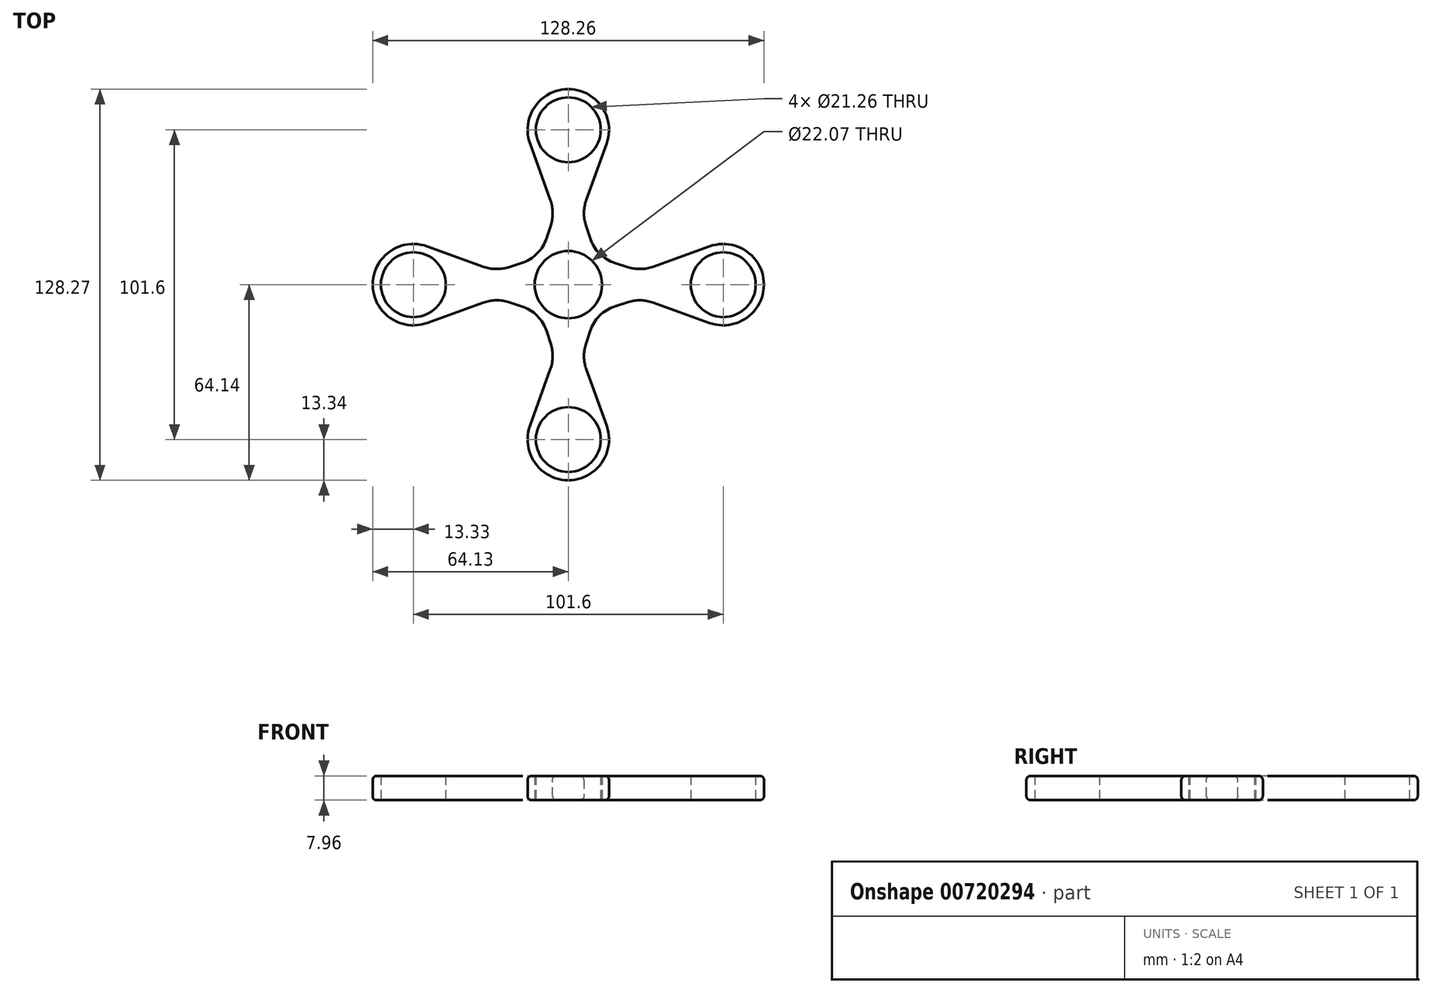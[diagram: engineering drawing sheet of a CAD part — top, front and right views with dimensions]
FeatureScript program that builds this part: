
annotation { "Feature Type Name" : "Feature", "Feature Type Description" : "" }
export const myFeature = defineFeature(function(context is Context, id is Id, definition is map)
    precondition{}
    {
        {
            var Q0;
            Q0=qCreatedBy(makeId("Top.planeOp"),FACE);
            var sketch = newSketch(context, id + "F0", { "sketchPlane" : qUnion([Q0])});
            skCircle(sketch, "E0", {"center": v(0, 0) * mm, "radius": 11.43 * mm});
            skCircle(sketch, "E1", {"center": v(0, 50.8) * mm, "radius": 13.34 * mm});
            skCircle(sketch, "E2", {"center": v(-50.8, 0) * mm, "radius": 13.34 * mm});
            skCircle(sketch, "E3", {"center": v(0, -50.8) * mm, "radius": 13.34 * mm});
            skCircle(sketch, "E4", {"center": v(50.8, 0) * mm, "radius": 13.34 * mm});
            skLineSegment(sketch, "E5", {"start": v(0, 37.47) * mm, "end": v(-10.89, 3.49) * mm});
            skLineSegment(sketch, "E6", {"start": v(0, 37.47) * mm, "end": v(10.89, 3.49) * mm});
            skLineSegment(sketch, "E7", {"start": v(-12.55, 46.28) * mm, "end": v(0, 11.43) * mm});
            skLineSegment(sketch, "E8", {"start": v(0, 11.43) * mm, "end": v(12.55, 46.28) * mm});
            skLineSegment(sketch, "E9", {"start": v(-46.28, 12.55) * mm, "end": v(-11.43, 0) * mm});
            skLineSegment(sketch, "E10", {"start": v(-11.43, 0) * mm, "end": v(-46.28, -12.55) * mm});
            skLineSegment(sketch, "E11", {"start": v(-37.46, 0) * mm, "end": v(-3.49, 10.89) * mm});
            skLineSegment(sketch, "E12", {"start": v(-37.47, 0) * mm, "end": v(-3.49, -10.89) * mm});
            skLineSegment(sketch, "E13", {"start": v(-12.55, -46.28) * mm, "end": v(0, -11.43) * mm});
            skLineSegment(sketch, "E14", {"start": v(0, -11.43) * mm, "end": v(12.55, -46.28) * mm});
            skLineSegment(sketch, "E15", {"start": v(-10.89, -3.49) * mm, "end": v(0, -37.47) * mm});
            skLineSegment(sketch, "E16", {"start": v(0, -37.46) * mm, "end": v(10.89, -3.49) * mm});
            skLineSegment(sketch, "E17", {"start": v(37.47, 0) * mm, "end": v(3.49, 10.89) * mm});
            skLineSegment(sketch, "E18", {"start": v(3.49, -10.89) * mm, "end": v(37.47, 0) * mm});
            skLineSegment(sketch, "E19", {"start": v(11.43, 0) * mm, "end": v(46.28, 12.55) * mm});
            skLineSegment(sketch, "E20", {"start": v(11.43, 0) * mm, "end": v(46.28, -12.55) * mm});
            skLineSegment(sketch, "E21", {"start": v(0, 50.8) * mm, "end": v(0, 0) * mm});
            skLineSegment(sketch, "E22", {"start": v(0, 0) * mm, "end": v(-50.8, 0) * mm});
            skLineSegment(sketch, "E23", {"start": v(0, 0) * mm, "end": v(0, -50.8) * mm});
            skLineSegment(sketch, "E24", {"start": v(0, 0) * mm, "end": v(50.8, 0) * mm});
            skSolve(sketch);
        }
        {
            var Q0;
            {var subQ0=sQuery(id+"F0.wireOp",EDGE,"E1");var subQ2=makeQuery(id+"F0.imprint","INTERSECT",VERTEX,{"derivedFrom":[subQ0,sQuery(id+"F0.wireOp",EDGE,"E7")]});Q0=makeQuery(id+"F0.imprint","IMPRINT",FACE,{"disambiguationData":[TD([[makeQuery(id+"F0.imprint","IMPRINT",EDGE,{"disambiguationData":[TD([[subQ2,1.0]])],"derivedFrom":subQ0}),1.0]])]});}
            var Q1;
            {var subQ1=sQuery(id+"F0.wireOp",EDGE,"E1");var subQ3=sQuery(id+"F0.wireOp",EDGE,"E7");var subQ4=makeQuery(id+"F0.imprint","INTERSECT",VERTEX,{"derivedFrom":[subQ1,subQ3]});Q1=makeQuery(id+"F0.imprint","IMPRINT",FACE,{"disambiguationData":[TD([[makeQuery(id+"F0.imprint","IMPRINT",EDGE,{"disambiguationData":[TD([[subQ4,-1.0]])],"derivedFrom":subQ3}),1.0]])]});}
            var Q2;
            {var subQ1=sQuery(id+"F0.wireOp",EDGE,"E1");var subQ3=sQuery(id+"F0.wireOp",EDGE,"E8");var subQ4=makeQuery(id+"F0.imprint","INTERSECT",VERTEX,{"derivedFrom":[subQ1,subQ3]});Q2=makeQuery(id+"F0.imprint","IMPRINT",FACE,{"disambiguationData":[TD([[makeQuery(id+"F0.imprint","IMPRINT",EDGE,{"disambiguationData":[TD([[subQ4,1.0]])],"derivedFrom":subQ3}),1.0]])]});}
            var Q3;
            {var subQ0=sQuery(id+"F0.wireOp",EDGE,"E9");var subQ1=sQuery(id+"F0.wireOp",EDGE,"E2");var subQ2=makeQuery(id+"F0.imprint","INTERSECT",VERTEX,{"derivedFrom":[subQ1,subQ0]});Q3=makeQuery(id+"F0.imprint","IMPRINT",FACE,{"disambiguationData":[TD([[makeQuery(id+"F0.imprint","IMPRINT",EDGE,{"disambiguationData":[TD([[subQ2,-1.0]])],"derivedFrom":subQ0}),-1.0]])]});}
            var Q4;
            {var subQ0=sQuery(id+"F0.wireOp",EDGE,"E10");var subQ1=sQuery(id+"F0.wireOp",EDGE,"E2");var subQ2=makeQuery(id+"F0.imprint","INTERSECT",VERTEX,{"derivedFrom":[subQ1,subQ0]});Q4=makeQuery(id+"F0.imprint","IMPRINT",FACE,{"disambiguationData":[TD([[makeQuery(id+"F0.imprint","IMPRINT",EDGE,{"disambiguationData":[TD([[subQ2,1.0]])],"derivedFrom":subQ0}),-1.0]])]});}
            var Q5;
            {var subQ0=sQuery(id+"F0.wireOp",EDGE,"E3");var subQ3=makeQuery(id+"F0.imprint","INTERSECT",VERTEX,{"derivedFrom":[subQ0,sQuery(id+"F0.wireOp",EDGE,"E13")]});Q5=makeQuery(id+"F0.imprint","IMPRINT",FACE,{"disambiguationData":[TD([[makeQuery(id+"F0.imprint","IMPRINT",EDGE,{"disambiguationData":[TD([[subQ3,-1.0]])],"derivedFrom":subQ0}),1.0]])]});}
            var Q6;
            {var subQ0=sQuery(id+"F0.wireOp",EDGE,"E14");var subQ1=sQuery(id+"F0.wireOp",EDGE,"E3");var subQ2=makeQuery(id+"F0.imprint","INTERSECT",VERTEX,{"derivedFrom":[subQ1,subQ0]});Q6=makeQuery(id+"F0.imprint","IMPRINT",FACE,{"disambiguationData":[TD([[makeQuery(id+"F0.imprint","IMPRINT",EDGE,{"disambiguationData":[TD([[subQ2,1.0]])],"derivedFrom":subQ0}),-1.0]])]});}
            var Q7;
            {var subQ0=sQuery(id+"F0.wireOp",EDGE,"E13");var subQ1=sQuery(id+"F0.wireOp",EDGE,"E3");var subQ2=makeQuery(id+"F0.imprint","INTERSECT",VERTEX,{"derivedFrom":[subQ1,subQ0]});Q7=makeQuery(id+"F0.imprint","IMPRINT",FACE,{"disambiguationData":[TD([[makeQuery(id+"F0.imprint","IMPRINT",EDGE,{"disambiguationData":[TD([[subQ2,-1.0]])],"derivedFrom":subQ0}),-1.0]])]});}
            var Q8;
            {var subQ0=sQuery(id+"F0.wireOp",EDGE,"E4");var subQ2=makeQuery(id+"F0.imprint","INTERSECT",VERTEX,{"derivedFrom":[subQ0,sQuery(id+"F0.wireOp",EDGE,"E19")]});Q8=makeQuery(id+"F0.imprint","IMPRINT",FACE,{"disambiguationData":[TD([[makeQuery(id+"F0.imprint","IMPRINT",EDGE,{"disambiguationData":[TD([[subQ2,1.0]])],"derivedFrom":subQ0}),1.0]])]});}
            var Q9;
            {var subQ1=sQuery(id+"F0.wireOp",EDGE,"E4");var subQ3=sQuery(id+"F0.wireOp",EDGE,"E19");var subQ4=makeQuery(id+"F0.imprint","INTERSECT",VERTEX,{"derivedFrom":[subQ1,subQ3]});Q9=makeQuery(id+"F0.imprint","IMPRINT",FACE,{"disambiguationData":[TD([[makeQuery(id+"F0.imprint","IMPRINT",EDGE,{"disambiguationData":[TD([[subQ4,1.0]])],"derivedFrom":subQ3}),-1.0]])]});}
            var Q10;
            {var subQ1=sQuery(id+"F0.wireOp",EDGE,"E4");var subQ3=sQuery(id+"F0.wireOp",EDGE,"E20");var subQ4=makeQuery(id+"F0.imprint","INTERSECT",VERTEX,{"derivedFrom":[subQ1,subQ3]});Q10=makeQuery(id+"F0.imprint","IMPRINT",FACE,{"disambiguationData":[TD([[makeQuery(id+"F0.imprint","IMPRINT",EDGE,{"disambiguationData":[TD([[subQ4,1.0]])],"derivedFrom":subQ3}),1.0]])]});}
            var Q11;
            {var subQ0=sQuery(id+"F0.wireOp",EDGE,"E6");var subQ1=sQuery(id+"F0.wireOp",EDGE,"E0");var subQ2=makeQuery(id+"F0.imprint","INTERSECT",VERTEX,{"derivedFrom":[subQ1,subQ0]});Q11=makeQuery(id+"F0.imprint","IMPRINT",FACE,{"disambiguationData":[TD([[makeQuery(id+"F0.imprint","IMPRINT",EDGE,{"disambiguationData":[TD([[subQ2,1.0]])],"derivedFrom":subQ0}),1.0]])]});}
            var Q12;
            {var subQ0=sQuery(id+"F0.wireOp",EDGE,"E6");var subQ1=sQuery(id+"F0.wireOp",EDGE,"E0");var subQ2=makeQuery(id+"F0.imprint","INTERSECT",VERTEX,{"derivedFrom":[subQ1,subQ0]});Q12=makeQuery(id+"F0.imprint","IMPRINT",FACE,{"disambiguationData":[TD([[makeQuery(id+"F0.imprint","IMPRINT",EDGE,{"disambiguationData":[TD([[subQ2,-1.0]])],"derivedFrom":subQ1}),-1.0]])]});}
            var Q13;
            {var subQ0=sQuery(id+"F0.wireOp",EDGE,"E8");var subQ5=sQuery(id+"F0.wireOp",EDGE,"E6");var subQ6=makeQuery(id+"F0.imprint","INTERSECT",VERTEX,{"derivedFrom":[subQ5,subQ0]});Q13=makeQuery(id+"F0.imprint","IMPRINT",FACE,{"disambiguationData":[TD([[makeQuery(id+"F0.imprint","IMPRINT",EDGE,{"disambiguationData":[TD([[subQ6,-1.0]])],"derivedFrom":subQ5}),-1.0]])]});}
            var Q14;
            {var subQ0=sQuery(id+"F0.wireOp",EDGE,"E7");var subQ5=sQuery(id+"F0.wireOp",EDGE,"E5");var subQ6=makeQuery(id+"F0.imprint","INTERSECT",VERTEX,{"derivedFrom":[subQ5,subQ0]});Q14=makeQuery(id+"F0.imprint","IMPRINT",FACE,{"disambiguationData":[TD([[makeQuery(id+"F0.imprint","IMPRINT",EDGE,{"disambiguationData":[TD([[subQ6,-1.0]])],"derivedFrom":subQ5}),1.0]])]});}
            var Q15;
            {var subQ0=sQuery(id+"F0.wireOp",EDGE,"E5");var subQ1=sQuery(id+"F0.wireOp",EDGE,"E0");var subQ2=makeQuery(id+"F0.imprint","INTERSECT",VERTEX,{"derivedFrom":[subQ1,subQ0]});Q15=makeQuery(id+"F0.imprint","IMPRINT",FACE,{"disambiguationData":[TD([[makeQuery(id+"F0.imprint","IMPRINT",EDGE,{"disambiguationData":[TD([[subQ2,1.0]])],"derivedFrom":subQ1}),-1.0]])]});}
            var Q16;
            {var subQ0=sQuery(id+"F0.wireOp",EDGE,"E5");var subQ1=sQuery(id+"F0.wireOp",EDGE,"E0");var subQ2=makeQuery(id+"F0.imprint","INTERSECT",VERTEX,{"derivedFrom":[subQ1,subQ0]});Q16=makeQuery(id+"F0.imprint","IMPRINT",FACE,{"disambiguationData":[TD([[makeQuery(id+"F0.imprint","IMPRINT",EDGE,{"disambiguationData":[TD([[subQ2,1.0]])],"derivedFrom":subQ0}),-1.0]])]});}
            var Q17;
            {var subQ0=sQuery(id+"F0.wireOp",EDGE,"E10");var subQ5=sQuery(id+"F0.wireOp",EDGE,"E12");var subQ6=makeQuery(id+"F0.imprint","INTERSECT",VERTEX,{"derivedFrom":[subQ0,subQ5]});Q17=makeQuery(id+"F0.imprint","IMPRINT",FACE,{"disambiguationData":[TD([[makeQuery(id+"F0.imprint","IMPRINT",EDGE,{"disambiguationData":[TD([[subQ6,-1.0]])],"derivedFrom":subQ5}),1.0]])]});}
            var Q18;
            {var subQ0=sQuery(id+"F0.wireOp",EDGE,"E12");var subQ1=sQuery(id+"F0.wireOp",EDGE,"E0");var subQ2=makeQuery(id+"F0.imprint","INTERSECT",VERTEX,{"derivedFrom":[subQ1,subQ0]});Q18=makeQuery(id+"F0.imprint","IMPRINT",FACE,{"disambiguationData":[TD([[makeQuery(id+"F0.imprint","IMPRINT",EDGE,{"disambiguationData":[TD([[subQ2,1.0]])],"derivedFrom":subQ1}),-1.0]])]});}
            var Q19;
            {var subQ0=sQuery(id+"F0.wireOp",EDGE,"E12");var subQ1=sQuery(id+"F0.wireOp",EDGE,"E0");var subQ2=makeQuery(id+"F0.imprint","INTERSECT",VERTEX,{"derivedFrom":[subQ1,subQ0]});Q19=makeQuery(id+"F0.imprint","IMPRINT",FACE,{"disambiguationData":[TD([[makeQuery(id+"F0.imprint","IMPRINT",EDGE,{"disambiguationData":[TD([[subQ2,1.0]])],"derivedFrom":subQ0}),-1.0]])]});}
            var Q20;
            {var subQ0=sQuery(id+"F0.wireOp",EDGE,"E14");var subQ5=sQuery(id+"F0.wireOp",EDGE,"E16");var subQ6=makeQuery(id+"F0.imprint","INTERSECT",VERTEX,{"derivedFrom":[subQ0,subQ5]});Q20=makeQuery(id+"F0.imprint","IMPRINT",FACE,{"disambiguationData":[TD([[makeQuery(id+"F0.imprint","IMPRINT",EDGE,{"disambiguationData":[TD([[subQ6,-1.0]])],"derivedFrom":subQ5}),1.0]])]});}
            var Q21;
            {var subQ0=sQuery(id+"F0.wireOp",EDGE,"E16");var subQ1=sQuery(id+"F0.wireOp",EDGE,"E0");var subQ2=makeQuery(id+"F0.imprint","INTERSECT",VERTEX,{"derivedFrom":[subQ1,subQ0]});Q21=makeQuery(id+"F0.imprint","IMPRINT",FACE,{"disambiguationData":[TD([[makeQuery(id+"F0.imprint","IMPRINT",EDGE,{"disambiguationData":[TD([[subQ2,1.0]])],"derivedFrom":subQ1}),-1.0]])]});}
            var Q22;
            {var subQ0=sQuery(id+"F0.wireOp",EDGE,"E16");var subQ1=sQuery(id+"F0.wireOp",EDGE,"E0");var subQ2=makeQuery(id+"F0.imprint","INTERSECT",VERTEX,{"derivedFrom":[subQ1,subQ0]});Q22=makeQuery(id+"F0.imprint","IMPRINT",FACE,{"disambiguationData":[TD([[makeQuery(id+"F0.imprint","IMPRINT",EDGE,{"disambiguationData":[TD([[subQ2,1.0]])],"derivedFrom":subQ0}),-1.0]])]});}
            var Q23;
            {var subQ1=sQuery(id+"F0.wireOp",EDGE,"E5");var subQ3=sQuery(id+"F0.wireOp",EDGE,"E7");var subQ4=makeQuery(id+"F0.imprint","INTERSECT",VERTEX,{"derivedFrom":[subQ1,subQ3]});Q23=makeQuery(id+"F0.imprint","IMPRINT",FACE,{"disambiguationData":[TD([[makeQuery(id+"F0.imprint","IMPRINT",EDGE,{"disambiguationData":[TD([[subQ4,1.0]])],"derivedFrom":subQ1}),1.0]])]});}
            var Q24;
            {var subQ1=sQuery(id+"F0.wireOp",EDGE,"E6");var subQ3=sQuery(id+"F0.wireOp",EDGE,"E8");var subQ4=makeQuery(id+"F0.imprint","INTERSECT",VERTEX,{"derivedFrom":[subQ1,subQ3]});Q24=makeQuery(id+"F0.imprint","IMPRINT",FACE,{"disambiguationData":[TD([[makeQuery(id+"F0.imprint","IMPRINT",EDGE,{"disambiguationData":[TD([[subQ4,1.0]])],"derivedFrom":subQ1}),-1.0]])]});}
            var Q25;
            {var subQ1=sQuery(id+"F0.wireOp",EDGE,"E9");var subQ3=sQuery(id+"F0.wireOp",EDGE,"E11");var subQ4=makeQuery(id+"F0.imprint","INTERSECT",VERTEX,{"derivedFrom":[subQ1,subQ3]});Q25=makeQuery(id+"F0.imprint","IMPRINT",FACE,{"disambiguationData":[TD([[makeQuery(id+"F0.imprint","IMPRINT",EDGE,{"disambiguationData":[TD([[subQ4,-1.0]])],"derivedFrom":subQ1}),-1.0]])]});}
            var Q26;
            {var subQ1=sQuery(id+"F0.wireOp",EDGE,"E10");var subQ3=sQuery(id+"F0.wireOp",EDGE,"E12");var subQ4=makeQuery(id+"F0.imprint","INTERSECT",VERTEX,{"derivedFrom":[subQ1,subQ3]});Q26=makeQuery(id+"F0.imprint","IMPRINT",FACE,{"disambiguationData":[TD([[makeQuery(id+"F0.imprint","IMPRINT",EDGE,{"disambiguationData":[TD([[subQ4,1.0]])],"derivedFrom":subQ1}),-1.0]])]});}
            var Q27;
            {var subQ1=sQuery(id+"F0.wireOp",EDGE,"E13");var subQ3=sQuery(id+"F0.wireOp",EDGE,"E15");var subQ4=makeQuery(id+"F0.imprint","INTERSECT",VERTEX,{"derivedFrom":[subQ1,subQ3]});Q27=makeQuery(id+"F0.imprint","IMPRINT",FACE,{"disambiguationData":[TD([[makeQuery(id+"F0.imprint","IMPRINT",EDGE,{"disambiguationData":[TD([[subQ4,-1.0]])],"derivedFrom":subQ1}),-1.0]])]});}
            var Q28;
            {var subQ1=sQuery(id+"F0.wireOp",EDGE,"E14");var subQ3=sQuery(id+"F0.wireOp",EDGE,"E16");var subQ4=makeQuery(id+"F0.imprint","INTERSECT",VERTEX,{"derivedFrom":[subQ1,subQ3]});Q28=makeQuery(id+"F0.imprint","IMPRINT",FACE,{"disambiguationData":[TD([[makeQuery(id+"F0.imprint","IMPRINT",EDGE,{"disambiguationData":[TD([[subQ4,1.0]])],"derivedFrom":subQ1}),-1.0]])]});}
            var Q29;
            {var subQ1=sQuery(id+"F0.wireOp",EDGE,"E17");var subQ3=sQuery(id+"F0.wireOp",EDGE,"E19");var subQ4=makeQuery(id+"F0.imprint","INTERSECT",VERTEX,{"derivedFrom":[subQ1,subQ3]});Q29=makeQuery(id+"F0.imprint","IMPRINT",FACE,{"disambiguationData":[TD([[makeQuery(id+"F0.imprint","IMPRINT",EDGE,{"disambiguationData":[TD([[subQ4,1.0]])],"derivedFrom":subQ1}),1.0]])]});}
            var Q30;
            {var subQ1=sQuery(id+"F0.wireOp",EDGE,"E18");var subQ3=sQuery(id+"F0.wireOp",EDGE,"E20");var subQ4=makeQuery(id+"F0.imprint","INTERSECT",VERTEX,{"derivedFrom":[subQ1,subQ3]});Q30=makeQuery(id+"F0.imprint","IMPRINT",FACE,{"disambiguationData":[TD([[makeQuery(id+"F0.imprint","IMPRINT",EDGE,{"disambiguationData":[TD([[subQ4,-1.0]])],"derivedFrom":subQ1}),1.0]])]});}
            var Q31;
            {var subQ1=sQuery(id+"F0.wireOp",EDGE,"E0");var subQ5=makeQuery(id+"F0.imprint","INTERSECT",VERTEX,{"derivedFrom":[subQ1,sQuery(id+"F0.wireOp",EDGE,"E5")]});Q31=makeQuery(id+"F0.imprint","IMPRINT",FACE,{"disambiguationData":[TD([[makeQuery(id+"F0.imprint","IMPRINT",EDGE,{"disambiguationData":[TD([[subQ5,1.0]])],"derivedFrom":subQ1}),1.0]])]});}
            var Q32;
            {var subQ0=sQuery(id+"F0.wireOp",EDGE,"E0");var subQ1=makeQuery(id+"F0.imprint","INTERSECT",VERTEX,{"derivedFrom":[subQ0,sQuery(id+"F0.wireOp",EDGE,"E12")]});Q32=makeQuery(id+"F0.imprint","IMPRINT",FACE,{"disambiguationData":[TD([[makeQuery(id+"F0.imprint","IMPRINT",EDGE,{"disambiguationData":[TD([[subQ1,1.0]])],"derivedFrom":subQ0}),1.0]])]});}
            var Q33;
            {var subQ1=sQuery(id+"F0.wireOp",EDGE,"E0");var subQ4=makeQuery(id+"F0.imprint","INTERSECT",VERTEX,{"derivedFrom":[subQ1,sQuery(id+"F0.wireOp",EDGE,"E6")]});Q33=makeQuery(id+"F0.imprint","IMPRINT",FACE,{"disambiguationData":[TD([[makeQuery(id+"F0.imprint","IMPRINT",EDGE,{"disambiguationData":[TD([[subQ4,-1.0]])],"derivedFrom":subQ1}),1.0]])]});}
            var Q34;
            {var subQ1=sQuery(id+"F0.wireOp",EDGE,"E0");var subQ5=makeQuery(id+"F0.imprint","INTERSECT",VERTEX,{"derivedFrom":[subQ1,sQuery(id+"F0.wireOp",EDGE,"E16")]});Q34=makeQuery(id+"F0.imprint","IMPRINT",FACE,{"disambiguationData":[TD([[makeQuery(id+"F0.imprint","IMPRINT",EDGE,{"disambiguationData":[TD([[subQ5,1.0]])],"derivedFrom":subQ1}),1.0]])]});}
            var Q35;
            {var subQ0=sQuery(id+"F0.wireOp",EDGE,"E2");var subQ1=makeQuery(id+"F0.imprint","INTERSECT",VERTEX,{"derivedFrom":[subQ0,sQuery(id+"F0.wireOp",EDGE,"E9")]});Q35=makeQuery(id+"F0.imprint","IMPRINT",FACE,{"disambiguationData":[TD([[makeQuery(id+"F0.imprint","IMPRINT",EDGE,{"disambiguationData":[TD([[subQ1,-1.0]])],"derivedFrom":subQ0}),1.0]])]});}
            extrude(context, id + "F1", {"entities" : qUnion([Q0, Q1, Q2, Q3, Q4, Q5, Q6, Q7, Q8, Q9, Q10, Q11, Q12, Q13, Q14, Q15, Q16, Q17, Q18, Q19, Q20, Q21, Q22, Q23, Q24, Q25, Q26, Q27, Q28, Q29, Q30, Q31, Q32, Q33, Q34, Q35]), "depth" : 7.95 * mm, "offsetDistance" : 25.4 * mm, "symmetric" : true});
        }
        {
            var Q0;
            Q0=makeQuery(id+"F1.opExtrude","SWEPT_EDGE",EDGE,{"disambiguationData":[OSD([sQuery(id+"F0.wireOp",EDGE,"E10"),sQuery(id+"F0.wireOp",EDGE,"E12")])]});
            var Q1;
            Q1=makeQuery(id+"F1.opExtrude","SWEPT_EDGE",EDGE,{"disambiguationData":[OSD([sQuery(id+"F0.wireOp",EDGE,"E12"),sQuery(id+"F0.wireOp",EDGE,"E15")])]});
            var Q2;
            Q2=makeQuery(id+"F1.opExtrude","SWEPT_EDGE",EDGE,{"disambiguationData":[OSD([sQuery(id+"F0.wireOp",EDGE,"E13"),sQuery(id+"F0.wireOp",EDGE,"E15")])]});
            var Q3;
            Q3=makeQuery(id+"F1.opExtrude","SWEPT_EDGE",EDGE,{"disambiguationData":[OSD([sQuery(id+"F0.wireOp",EDGE,"E14"),sQuery(id+"F0.wireOp",EDGE,"E16")])]});
            var Q4;
            Q4=makeQuery(id+"F1.opExtrude","SWEPT_EDGE",EDGE,{"disambiguationData":[OSD([sQuery(id+"F0.wireOp",EDGE,"E16"),sQuery(id+"F0.wireOp",EDGE,"E18")])]});
            var Q5;
            Q5=makeQuery(id+"F1.opExtrude","SWEPT_EDGE",EDGE,{"disambiguationData":[OSD([sQuery(id+"F0.wireOp",EDGE,"E18"),sQuery(id+"F0.wireOp",EDGE,"E20")])]});
            var Q6;
            Q6=makeQuery(id+"F1.opExtrude","SWEPT_EDGE",EDGE,{"disambiguationData":[OSD([sQuery(id+"F0.wireOp",EDGE,"E17"),sQuery(id+"F0.wireOp",EDGE,"E19")])]});
            var Q7;
            Q7=makeQuery(id+"F1.opExtrude","SWEPT_EDGE",EDGE,{"disambiguationData":[OSD([sQuery(id+"F0.wireOp",EDGE,"E6"),sQuery(id+"F0.wireOp",EDGE,"E17")])]});
            var Q8;
            Q8=makeQuery(id+"F1.opExtrude","SWEPT_EDGE",EDGE,{"disambiguationData":[OSD([sQuery(id+"F0.wireOp",EDGE,"E6"),sQuery(id+"F0.wireOp",EDGE,"E8")])]});
            var Q9;
            Q9=makeQuery(id+"F1.opExtrude","SWEPT_EDGE",EDGE,{"disambiguationData":[OSD([sQuery(id+"F0.wireOp",EDGE,"E5"),sQuery(id+"F0.wireOp",EDGE,"E11")])]});
            var Q10;
            Q10=makeQuery(id+"F1.opExtrude","SWEPT_EDGE",EDGE,{"disambiguationData":[OSD([sQuery(id+"F0.wireOp",EDGE,"E9"),sQuery(id+"F0.wireOp",EDGE,"E11")])]});
            var Q11;
            Q11=makeQuery(id+"F1.opExtrude","SWEPT_EDGE",EDGE,{"disambiguationData":[OSD([sQuery(id+"F0.wireOp",EDGE,"E5"),sQuery(id+"F0.wireOp",EDGE,"E7")])]});
            fillet(context, id + "F2", {"entities" : qUnion([Q0, Q1, Q2, Q3, Q4, Q5, Q6, Q7, Q8, Q9, Q10, Q11]), "radius" : 12.7 * mm, "tangentPropagation" : true, "allowEdgeOverflow" : false});
        }
        {
            var Q0;
            Q0=makeQuery(id+"F1.opExtrude","CAP_FACE",FACE,{"disambiguationData":[OSD([sQuery(id+"F0.wireOp",EDGE,"E1"),sQuery(id+"F0.wireOp",EDGE,"E2"),sQuery(id+"F0.wireOp",EDGE,"E3"),sQuery(id+"F0.wireOp",EDGE,"E4"),sQuery(id+"F0.wireOp",EDGE,"E5"),sQuery(id+"F0.wireOp",EDGE,"E6"),sQuery(id+"F0.wireOp",EDGE,"E7"),sQuery(id+"F0.wireOp",EDGE,"E8"),sQuery(id+"F0.wireOp",EDGE,"E9"),sQuery(id+"F0.wireOp",EDGE,"E10"),sQuery(id+"F0.wireOp",EDGE,"E11"),sQuery(id+"F0.wireOp",EDGE,"E12"),sQuery(id+"F0.wireOp",EDGE,"E13"),sQuery(id+"F0.wireOp",EDGE,"E14"),sQuery(id+"F0.wireOp",EDGE,"E15"),sQuery(id+"F0.wireOp",EDGE,"E16"),sQuery(id+"F0.wireOp",EDGE,"E17"),sQuery(id+"F0.wireOp",EDGE,"E18"),sQuery(id+"F0.wireOp",EDGE,"E19"),sQuery(id+"F0.wireOp",EDGE,"E20")])],"isStart":true});
            var sketch = newSketch(context, id + "F3", { "sketchPlane" : qUnion([Q0])});
            skCircle(sketch, "E25", {"center": v(0, 0) * mm, "radius": 11.04 * mm});
            skCircle(sketch, "E26", {"center": v(-50.8, 0) * mm, "radius": 10.63 * mm});
            skCircle(sketch, "E27", {"center": v(0, 50.8) * mm, "radius": 10.63 * mm});
            skCircle(sketch, "E28", {"center": v(50.8, 0) * mm, "radius": 10.63 * mm});
            skCircle(sketch, "E29", {"center": v(0, -50.8) * mm, "radius": 10.63 * mm});
            skSolve(sketch);
        }
        {
            var Q0;
            Q0=makeQuery(id+"F3.imprint","IMPRINT",FACE,{"disambiguationData":[TD([[makeQuery(id+"F3.imprint","IMPRINT",EDGE,{"derivedFrom":sQuery(id+"F3.wireOp",EDGE,"E26")}),1.0]])]});
            var Q1;
            Q1=makeQuery(id+"F3.imprint","IMPRINT",FACE,{"disambiguationData":[TD([[makeQuery(id+"F3.imprint","IMPRINT",EDGE,{"derivedFrom":sQuery(id+"F3.wireOp",EDGE,"E25")}),1.0]])]});
            var Q2;
            Q2=makeQuery(id+"F3.imprint","IMPRINT",FACE,{"disambiguationData":[TD([[makeQuery(id+"F3.imprint","IMPRINT",EDGE,{"derivedFrom":sQuery(id+"F3.wireOp",EDGE,"E28")}),1.0]])]});
            var Q3;
            Q3=makeQuery(id+"F3.imprint","IMPRINT",FACE,{"disambiguationData":[TD([[makeQuery(id+"F3.imprint","IMPRINT",EDGE,{"derivedFrom":sQuery(id+"F3.wireOp",EDGE,"E27")}),1.0]])]});
            var Q4;
            Q4=makeQuery(id+"F3.imprint","IMPRINT",FACE,{"disambiguationData":[TD([[makeQuery(id+"F3.imprint","IMPRINT",EDGE,{"derivedFrom":sQuery(id+"F3.wireOp",EDGE,"E29")}),1.0]])]});
            var Q5;
            Q5=makeQuery(id+"F1.opExtrude","CAP_FACE",FACE,{"disambiguationData":[OSD([sQuery(id+"F0.wireOp",EDGE,"E1"),sQuery(id+"F0.wireOp",EDGE,"E2"),sQuery(id+"F0.wireOp",EDGE,"E3"),sQuery(id+"F0.wireOp",EDGE,"E4"),sQuery(id+"F0.wireOp",EDGE,"E5"),sQuery(id+"F0.wireOp",EDGE,"E6"),sQuery(id+"F0.wireOp",EDGE,"E7"),sQuery(id+"F0.wireOp",EDGE,"E8"),sQuery(id+"F0.wireOp",EDGE,"E9"),sQuery(id+"F0.wireOp",EDGE,"E10"),sQuery(id+"F0.wireOp",EDGE,"E11"),sQuery(id+"F0.wireOp",EDGE,"E12"),sQuery(id+"F0.wireOp",EDGE,"E13"),sQuery(id+"F0.wireOp",EDGE,"E14"),sQuery(id+"F0.wireOp",EDGE,"E15"),sQuery(id+"F0.wireOp",EDGE,"E16"),sQuery(id+"F0.wireOp",EDGE,"E17"),sQuery(id+"F0.wireOp",EDGE,"E18"),sQuery(id+"F0.wireOp",EDGE,"E19"),sQuery(id+"F0.wireOp",EDGE,"E20")])],"isStart":false});
            extrude(context, id + "F4", {"entities" : qUnion([Q0, Q1, Q2, Q3, Q4]), "operationType" : NewBodyOperationType.REMOVE, "endBound" : BoundingType.UP_TO_SURFACE, "oppositeDirection" : true, "depth" : 25.4 * mm, "endBoundEntityFace" : qUnion([Q5]), "offsetDistance" : 25.4 * mm});
        }
        {
            var Q0;
            Q0=makeQuery(id+"F1.opExtrude","CAP_EDGE",EDGE,{"disambiguationData":[OSD([sQuery(id+"F0.wireOp",EDGE,"E10")])],"isStart":false});
            fillet(context, id + "F5", {"entities" : qUnion([Q0]), "radius" : 1.27 * mm, "tangentPropagation" : true, "allowEdgeOverflow" : false});
        }
        {
            var Q0;
            Q0=makeQuery(id+"F1.opExtrude","CAP_EDGE",EDGE,{"disambiguationData":[OSD([sQuery(id+"F0.wireOp",EDGE,"E14")])],"isStart":true});
            fillet(context, id + "F6", {"entities" : qUnion([Q0]), "radius" : 1.27 * mm, "tangentPropagation" : true, "allowEdgeOverflow" : false});
        }
    });
